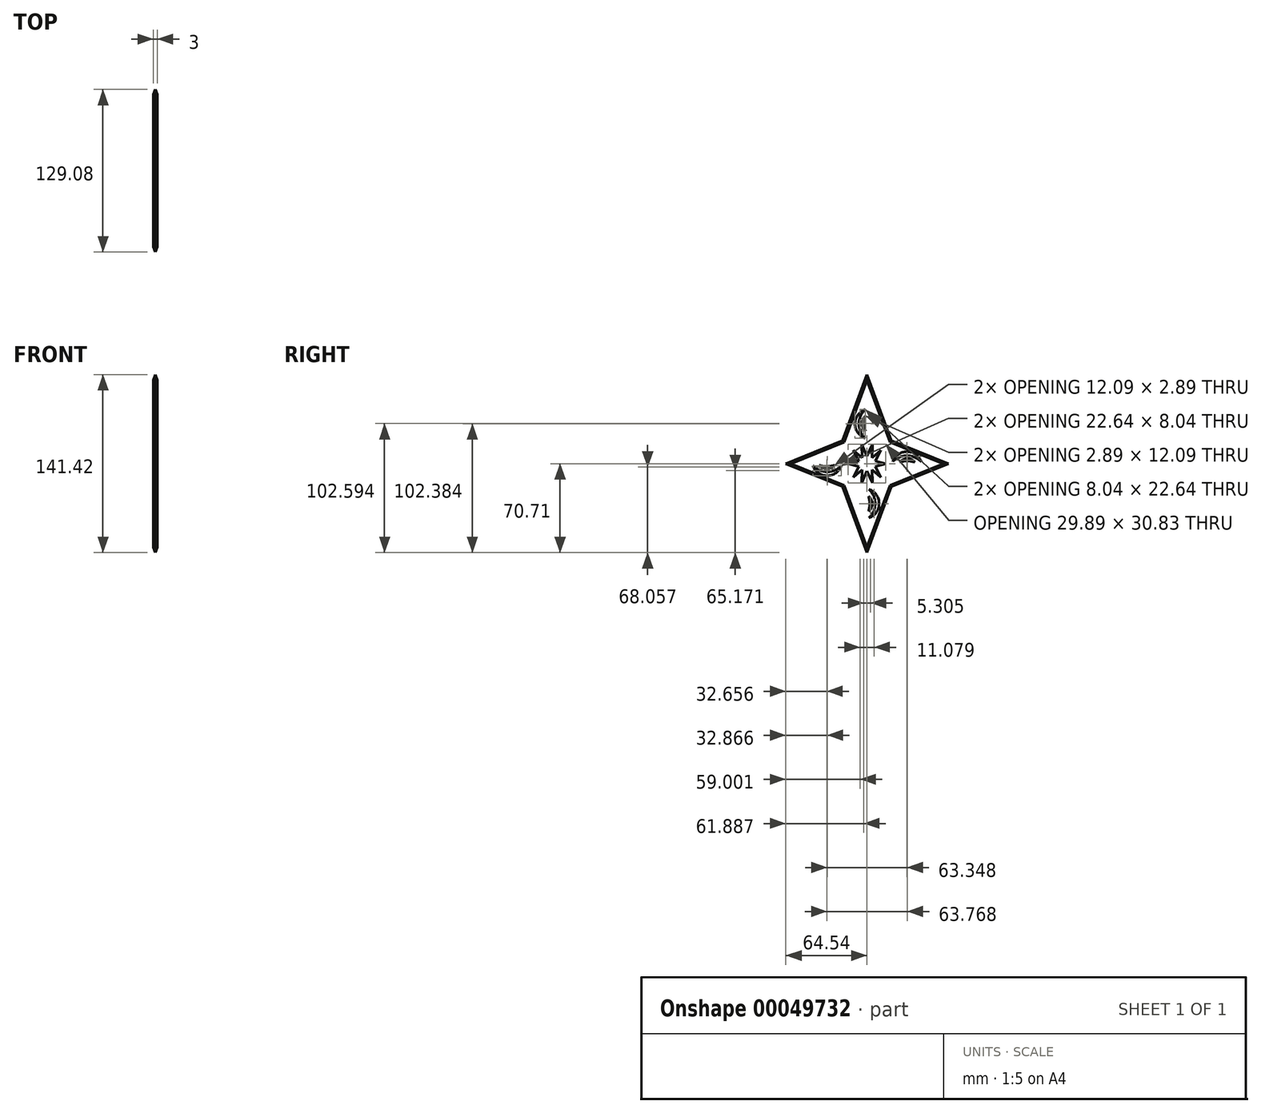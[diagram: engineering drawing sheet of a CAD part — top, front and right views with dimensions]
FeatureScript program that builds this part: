
annotation { "Feature Type Name" : "Feature", "Feature Type Description" : "" }
export const myFeature = defineFeature(function(context is Context, id is Id, definition is map)
    precondition{}
    {
        {
            var Q0;
            Q0=qCreatedBy(makeId("Right.planeOp"),FACE);
            var sketch = newSketch(context, id + "F0", { "sketchPlane" : qUnion([Q0])});
            skLineSegment(sketch, "E0", {"start": v(0, -70.7) * mm, "end": v(-19.36, -18.32) * mm});
            skLineSegment(sketch, "E1", {"start": v(-19.36, -18.32) * mm, "end": v(-64.54, 0) * mm});
            skLineSegment(sketch, "E2.MirrorCS", {"start": v(0, -70.7) * mm, "end": v(19.36, -18.32) * mm});
            skLineSegment(sketch, "E3.MirrorCS", {"start": v(19.36, -18.32) * mm, "end": v(64.54, 0) * mm});
            skLineSegment(sketch, "E4.MirrorCS", {"start": v(-19.36, 18.32) * mm, "end": v(-64.54, 0) * mm});
            skLineSegment(sketch, "E5.MirrorCS", {"start": v(0, 70.7) * mm, "end": v(-19.36, 18.32) * mm});
            skLineSegment(sketch, "E6.MirrorCS", {"start": v(0, 70.7) * mm, "end": v(19.36, 18.32) * mm});
            skLineSegment(sketch, "E7.MirrorCS", {"start": v(19.36, 18.32) * mm, "end": v(64.54, 0) * mm});
            skSolve(sketch);
        }
        {
            var Q0;
            Q0 = qSketchRegion(id + "F0", true);
            extrude(context, id + "F1", {"entities" : qUnion([Q0]), "depth" : 3 * mm});
        }
        {
            var Q0;
            Q0=makeQuery(id+"F1.opExtrude","CAP_EDGE",EDGE,{"disambiguationData":[OSD([sQuery(id+"F0.wireOp",EDGE,"E4.MirrorCS")])],"isStart":false});
            var Q1;
            Q1=makeQuery(id+"F1.opExtrude","CAP_EDGE",EDGE,{"disambiguationData":[OSD([sQuery(id+"F0.wireOp",EDGE,"E5.MirrorCS")])],"isStart":false});
            var Q2;
            Q2=makeQuery(id+"F1.opExtrude","CAP_EDGE",EDGE,{"disambiguationData":[OSD([sQuery(id+"F0.wireOp",EDGE,"E5.MirrorCS")])],"isStart":true});
            var Q3;
            Q3=makeQuery(id+"F1.opExtrude","CAP_EDGE",EDGE,{"disambiguationData":[OSD([sQuery(id+"F0.wireOp",EDGE,"E4.MirrorCS")])],"isStart":true});
            var Q4;
            Q4=makeQuery(id+"F1.opExtrude","CAP_EDGE",EDGE,{"disambiguationData":[OSD([sQuery(id+"F0.wireOp",EDGE,"E1")])],"isStart":true});
            var Q5;
            Q5=makeQuery(id+"F1.opExtrude","CAP_EDGE",EDGE,{"disambiguationData":[OSD([sQuery(id+"F0.wireOp",EDGE,"E1")])],"isStart":false});
            var Q6;
            Q6=makeQuery(id+"F1.opExtrude","CAP_EDGE",EDGE,{"disambiguationData":[OSD([sQuery(id+"F0.wireOp",EDGE,"E0")])],"isStart":true});
            var Q7;
            Q7=makeQuery(id+"F1.opExtrude","CAP_EDGE",EDGE,{"disambiguationData":[OSD([sQuery(id+"F0.wireOp",EDGE,"E0")])],"isStart":false});
            var Q8;
            Q8=makeQuery(id+"F1.opExtrude","CAP_EDGE",EDGE,{"disambiguationData":[OSD([sQuery(id+"F0.wireOp",EDGE,"E2.MirrorCS")])],"isStart":false});
            var Q9;
            Q9=makeQuery(id+"F1.opExtrude","CAP_EDGE",EDGE,{"disambiguationData":[OSD([sQuery(id+"F0.wireOp",EDGE,"E2.MirrorCS")])],"isStart":true});
            var Q10;
            Q10=makeQuery(id+"F1.opExtrude","CAP_EDGE",EDGE,{"disambiguationData":[OSD([sQuery(id+"F0.wireOp",EDGE,"E3.MirrorCS")])],"isStart":false});
            var Q11;
            Q11=makeQuery(id+"F1.opExtrude","CAP_EDGE",EDGE,{"disambiguationData":[OSD([sQuery(id+"F0.wireOp",EDGE,"E3.MirrorCS")])],"isStart":true});
            var Q12;
            Q12=makeQuery(id+"F1.opExtrude","CAP_EDGE",EDGE,{"disambiguationData":[OSD([sQuery(id+"F0.wireOp",EDGE,"E6.MirrorCS")])],"isStart":true});
            var Q13;
            Q13=makeQuery(id+"F1.opExtrude","CAP_EDGE",EDGE,{"disambiguationData":[OSD([sQuery(id+"F0.wireOp",EDGE,"E6.MirrorCS")])],"isStart":false});
            var Q14;
            Q14=makeQuery(id+"F1.opExtrude","CAP_EDGE",EDGE,{"disambiguationData":[OSD([sQuery(id+"F0.wireOp",EDGE,"E7.MirrorCS")])],"isStart":false});
            var Q15;
            Q15=makeQuery(id+"F1.opExtrude","CAP_EDGE",EDGE,{"disambiguationData":[OSD([sQuery(id+"F0.wireOp",EDGE,"E7.MirrorCS")])],"isStart":true});
            chamfer(context, id + "F2", {"entities" : qUnion([Q0, Q1, Q2, Q3, Q4, Q5, Q6, Q7, Q8, Q9, Q10, Q11, Q12, Q13, Q14, Q15]), "width" : 1.5 * mm, "tangentPropagation" : true});
        }
        {
            var Q0;
            Q0=qCreatedBy(makeId("Right.planeOp"),FACE);
            var sketch = newSketch(context, id + "F3", { "sketchPlane" : qUnion([Q0])});
            skLineSegment(sketch, "E8", {"start": v(0, -5.89) * mm, "end": v(4.3, -15.41) * mm});
            skLineSegment(sketch, "E9", {"start": v(4.3, -15.41) * mm, "end": v(4.11, -4.76) * mm});
            skLineSegment(sketch, "E10.MirrorCS", {"start": v(0, -5.89) * mm, "end": v(-4.3, -15.41) * mm});
            skLineSegment(sketch, "E11.MirrorCS", {"start": v(-4.3, -15.41) * mm, "end": v(-4.11, -4.76) * mm});
            skLineSegment(sketch, "E12.MirrorCS", {"start": v(-4.3, 15.41) * mm, "end": v(-4.11, 4.76) * mm});
            skLineSegment(sketch, "E13.MirrorCS", {"start": v(0, 5.89) * mm, "end": v(-4.3, 15.41) * mm});
            skLineSegment(sketch, "E14.MirrorCS", {"start": v(0, 5.89) * mm, "end": v(4.3, 15.41) * mm});
            skLineSegment(sketch, "E15.MirrorCS", {"start": v(4.3, 15.41) * mm, "end": v(4.11, 4.76) * mm});
            skLineSegment(sketch, "E16", {"start": v(-4.11, -4.76) * mm, "end": v(-10.84, -10.74) * mm});
            skLineSegment(sketch, "E17", {"start": v(-10.84, -10.74) * mm, "end": v(-6.54, -2.15) * mm});
            skLineSegment(sketch, "E18", {"start": v(-6.54, -2.15) * mm, "end": v(-14.95, 0) * mm});
            skLineSegment(sketch, "E19.MirrorCS", {"start": v(-6.54, 2.15) * mm, "end": v(-14.95, 0) * mm});
            skLineSegment(sketch, "E20.MirrorCS", {"start": v(-10.84, 10.74) * mm, "end": v(-6.54, 2.15) * mm});
            skLineSegment(sketch, "E21.MirrorCS", {"start": v(-4.11, 4.76) * mm, "end": v(-10.84, 10.74) * mm});
            skLineSegment(sketch, "E22.MirrorCS", {"start": v(6.54, 2.15) * mm, "end": v(14.95, 0) * mm});
            skLineSegment(sketch, "E23.MirrorCS", {"start": v(10.84, 10.74) * mm, "end": v(6.54, 2.15) * mm});
            skLineSegment(sketch, "E24.MirrorCS", {"start": v(4.11, 4.76) * mm, "end": v(10.84, 10.74) * mm});
            skLineSegment(sketch, "E25.MirrorCS", {"start": v(10.84, -10.74) * mm, "end": v(6.54, -2.15) * mm});
            skLineSegment(sketch, "E26.MirrorCS", {"start": v(4.11, -4.76) * mm, "end": v(10.84, -10.74) * mm});
            skLineSegment(sketch, "E27.MirrorCS", {"start": v(6.54, -2.15) * mm, "end": v(14.95, 0) * mm});
            skSolve(sketch);
        }
        {
            var Q0;
            Q0 = qSketchRegion(id + "F3", true);
            extrude(context, id + "F4", {"entities" : qUnion([Q0]), "operationType" : NewBodyOperationType.REMOVE, "depth" : 25 * mm});
        }
        {
            var Q0;
            Q0=qCreatedBy(makeId("Right.planeOp"),FACE);
            var sketch = newSketch(context, id + "F5", { "sketchPlane" : qUnion([Q0])});
            skArc(sketch, "E28", {"start": v(1.2, -37.93) * mm, "mid": v(4.1, -31.88) * mm, "end": v(1.2, -25.84) * mm});
            skArc(sketch, "E29", {"start": v(1.2, -37.93) * mm, "mid": v(2.13, -31.88) * mm, "end": v(1.2, -25.84) * mm});
            skArc(sketch, "E30", {"start": v(1.52, -43) * mm, "mid": v(9.56, -31.67) * mm, "end": v(1.52, -20.35) * mm});
            skArc(sketch, "E31", {"start": v(1.52, -43) * mm, "mid": v(6.41, -31.67) * mm, "end": v(1.52, -20.35) * mm});
            skArc(sketch, "E32.MirrorCS", {"start": v(-1.2, -37.93) * mm, "mid": v(-4.1, -31.88) * mm, "end": v(-1.2, -25.84) * mm});
            skArc(sketch, "E33.MirrorCS", {"start": v(-1.2, -37.93) * mm, "mid": v(-2.13, -31.88) * mm, "end": v(-1.2, -25.84) * mm});
            skArc(sketch, "E34.MirrorCS", {"start": v(-1.52, -43) * mm, "mid": v(-6.41, -31.67) * mm, "end": v(-1.52, -20.35) * mm});
            skArc(sketch, "E35.MirrorCS", {"start": v(-1.52, -43) * mm, "mid": v(-9.56, -31.67) * mm, "end": v(-1.52, -20.35) * mm});
            skSolve(sketch);
        }
        {
            var Q0;
            Q0=makeQuery(id+"F5.imprint","IMPRINT",FACE,{"disambiguationData":[TD([[makeQuery(id+"F5.imprint","IMPRINT",EDGE,{"derivedFrom":sQuery(id+"F5.wireOp",EDGE,"E34.MirrorCS")}),1.0]])]});
            var Q1;
            Q1=makeQuery(id+"F5.imprint","IMPRINT",FACE,{"disambiguationData":[TD([[makeQuery(id+"F5.imprint","IMPRINT",EDGE,{"derivedFrom":sQuery(id+"F5.wireOp",EDGE,"E32.MirrorCS")}),-1.0]])]});
            var Q2;
            Q2=makeQuery(id+"F5.imprint","IMPRINT",FACE,{"disambiguationData":[TD([[makeQuery(id+"F5.imprint","IMPRINT",EDGE,{"derivedFrom":sQuery(id+"F5.wireOp",EDGE,"E30")}),1.0]])]});
            var Q3;
            Q3=makeQuery(id+"F5.imprint","IMPRINT",FACE,{"disambiguationData":[TD([[makeQuery(id+"F5.imprint","IMPRINT",EDGE,{"derivedFrom":sQuery(id+"F5.wireOp",EDGE,"E28")}),1.0]])]});
            extrude(context, id + "F6", {"entities" : qUnion([Q0, Q1, Q2, Q3]), "operationType" : NewBodyOperationType.REMOVE, "endBound" : BoundingType.THROUGH_ALL, "depth" : 2 * mm});
        }
        {
            var Q0;
            Q0=qCreatedBy(makeId("Front.planeOp"),FACE);
            var sketch = newSketch(context, id + "F7", { "sketchPlane" : qUnion([Q0])});
            skLineSegment(sketch, "E36", {"start": v(0, 0) * mm, "end": v(-49.38, 0) * mm});
            skSolve(sketch);
        }
        {
            var Q0;
            Q0=makeQuery(id+"F1.opExtrude","SWEPT_BODY",BODY,{"disambiguationData":[OSD([sQuery(id+"F0.wireOp",EDGE,"E0"),sQuery(id+"F0.wireOp",EDGE,"E1"),sQuery(id+"F0.wireOp",EDGE,"E2.MirrorCS"),sQuery(id+"F0.wireOp",EDGE,"E3.MirrorCS"),sQuery(id+"F0.wireOp",EDGE,"E4.MirrorCS"),sQuery(id+"F0.wireOp",EDGE,"E5.MirrorCS"),sQuery(id+"F0.wireOp",EDGE,"E6.MirrorCS"),sQuery(id+"F0.wireOp",EDGE,"E7.MirrorCS")])]});
            var Q1;
            Q1=makeQuery(id+"F6.boolean.opBoolean","COPY",FACE,{"derivedFrom":makeQuery(id+"F6.opExtrude","SWEPT_FACE",FACE,{"disambiguationData":[OSD([sQuery(id+"F5.wireOp",EDGE,"E35.MirrorCS")])]})});
            var Q2;
            Q2=makeQuery(id+"F6.boolean.opBoolean","COPY",FACE,{"derivedFrom":makeQuery(id+"F6.opExtrude","SWEPT_FACE",FACE,{"disambiguationData":[OSD([sQuery(id+"F5.wireOp",EDGE,"E32.MirrorCS")])]})});
            var Q3;
            Q3=makeQuery(id+"F6.boolean.opBoolean","COPY",FACE,{"derivedFrom":makeQuery(id+"F6.opExtrude","SWEPT_FACE",FACE,{"disambiguationData":[OSD([sQuery(id+"F5.wireOp",EDGE,"E29")])]})});
            var Q4;
            Q4=makeQuery(id+"F6.boolean.opBoolean","COPY",FACE,{"derivedFrom":makeQuery(id+"F6.opExtrude","SWEPT_FACE",FACE,{"disambiguationData":[OSD([sQuery(id+"F5.wireOp",EDGE,"E31")])]})});
            var Q5;
            Q5=makeQuery(id+"F6.boolean.opBoolean","COPY",FACE,{"derivedFrom":makeQuery(id+"F6.opExtrude","SWEPT_FACE",FACE,{"disambiguationData":[OSD([sQuery(id+"F5.wireOp",EDGE,"E34.MirrorCS")])]})});
            var Q6;
            Q6=makeQuery(id+"F6.boolean.opBoolean","COPY",FACE,{"derivedFrom":makeQuery(id+"F6.opExtrude","SWEPT_FACE",FACE,{"disambiguationData":[OSD([sQuery(id+"F5.wireOp",EDGE,"E33.MirrorCS")])]})});
            var Q7;
            Q7=makeQuery(id+"F6.boolean.opBoolean","COPY",FACE,{"derivedFrom":makeQuery(id+"F6.opExtrude","SWEPT_FACE",FACE,{"disambiguationData":[OSD([sQuery(id+"F5.wireOp",EDGE,"E28")])]})});
            var Q8;
            Q8=makeQuery(id+"F6.boolean.opBoolean","COPY",FACE,{"derivedFrom":makeQuery(id+"F6.opExtrude","SWEPT_FACE",FACE,{"disambiguationData":[OSD([sQuery(id+"F5.wireOp",EDGE,"E30")])]})});
            var Q9;
            Q9=sQuery(id+"F7.wireOp",EDGE,"E36");
            circularPattern(context, id + "F8", {"operationType" : NewBodyOperationType.REMOVE, "faces" : qUnion([Q1, Q2, Q3, Q4, Q5, Q6, Q7, Q8]), "axis" : qUnion([Q9]), "angle" : 360 * degree, "instanceCount" : 4, "equalSpace" : true, "patternType" : PatternType.FACE});
        }
    });
